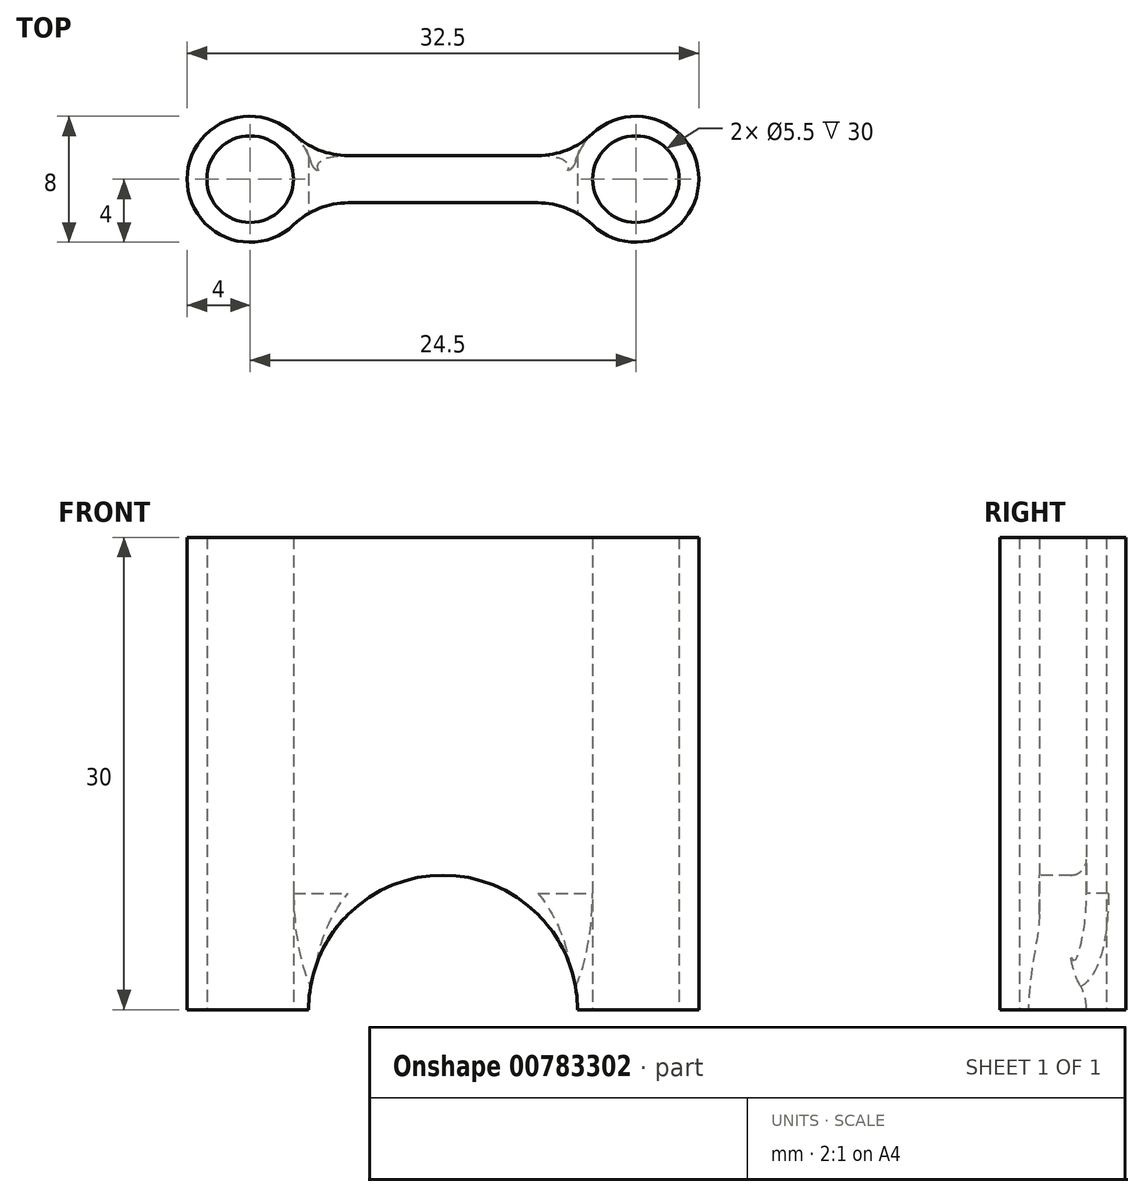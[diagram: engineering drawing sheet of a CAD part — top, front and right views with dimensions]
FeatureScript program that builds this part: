
annotation { "Feature Type Name" : "Feature", "Feature Type Description" : "" }
export const myFeature = defineFeature(function(context is Context, id is Id, definition is map)
    precondition{}
    {
        {
            var Q0;
            Q0=qCreatedBy(makeId("Top.planeOp"),FACE);
            var sketch = newSketch(context, id + "F0", { "sketchPlane" : qUnion([Q0])});
            skPoint(sketch, "E0", {"position": v(-12.25, 0) * mm});
            skPoint(sketch, "E1", {"position": v(12.25, 0) * mm});
            skCircle(sketch, "E2", {"center": v(-12.25, 0) * mm, "radius": 2.75 * mm});
            skCircle(sketch, "E3", {"center": v(12.25, 0) * mm, "radius": 2.75 * mm});
            skCircle(sketch, "E4", {"center": v(-12.25, 0) * mm, "radius": 4 * mm});
            skCircle(sketch, "E5", {"center": v(12.25, 0) * mm, "radius": 4 * mm});
            skLineSegment(sketch, "E6", {"start": v(-8.54, 1.5) * mm, "end": v(8.54, 1.5) * mm});
            skLineSegment(sketch, "E7", {"start": v(8.54, -1.5) * mm, "end": v(-8.54, -1.5) * mm});
            skPoint(sketch, "E8", {"position": v(-12.25, -4) * mm});
            skPoint(sketch, "E9", {"position": v(12.25, -4) * mm});
            skPoint(sketch, "E10", {"position": v(12.25, -8.25) * mm});
            skSolve(sketch);
        }
        {
            var Q0;
            Q0=makeQuery(id+"F0.imprint","IMPRINT",FACE,{"disambiguationData":[TD([[makeQuery(id+"F0.imprint","IMPRINT",EDGE,{"derivedFrom":sQuery(id+"F0.wireOp",EDGE,"E2")}),-1.0]])]});
            var Q1;
            Q1=makeQuery(id+"F0.imprint","IMPRINT",FACE,{"disambiguationData":[TD([[makeQuery(id+"F0.imprint","IMPRINT",EDGE,{"derivedFrom":sQuery(id+"F0.wireOp",EDGE,"E3")}),-1.0]])]});
            var Q2;
            {var subQ0=sQuery(id+"F0.wireOp",EDGE,"E6");Q2=makeQuery(id+"F0.imprint","IMPRINT",FACE,{"disambiguationData":[TD([[makeQuery(id+"F0.imprint","IMPRINT",EDGE,{"derivedFrom":subQ0}),-1.0]])]});}
            extrude(context, id + "F1", {"entities" : qUnion([Q0, Q1, Q2]), "depth" : 30 * mm, "offsetDistance" : 25 * mm});
        }
        {
            var Q0;
            Q0=makeQuery(id+"F1.opExtrude","SWEPT_FACE",FACE,{"disambiguationData":[OSD([sQuery(id+"F0.wireOp",EDGE,"E7")])]});
            var sketch = newSketch(context, id + "F2", { "sketchPlane" : qUnion([Q0])});
            skArc(sketch, "E11", {"start": v(8.54, 0) * mm, "mid": v(0, 8.54) * mm, "end": v(-8.54, 0) * mm});
            skArc(sketch, "E12", {"start": v(-9.91, 30) * mm, "mid": v(-0.01, 19.11) * mm, "end": v(9.9, 30) * mm});
            skSolve(sketch);
        }
        {
            var Q0;
            Q0=makeQuery(id+"F2.imprint","IMPRINT",FACE,{"disambiguationData":[TD([[makeQuery(id+"F2.imprint","IMPRINT",EDGE,{"derivedFrom":sQuery(id+"F2.wireOp",EDGE,"35eb756d-b366-46d8-bd96-28ccdfe76fae")}),1.0]])]});
            var Q1;
            Q1=makeQuery(id+"F2.imprint","IMPRINT",FACE,{"disambiguationData":[TD([[makeQuery(id+"F2.imprint","IMPRINT",EDGE,{"derivedFrom":sQuery(id+"F2.wireOp",EDGE,"E11")}),1.0]])]});
            extrude(context, id + "F3", {"entities" : qUnion([Q0, Q1]), "operationType" : NewBodyOperationType.REMOVE, "endBound" : BoundingType.THROUGH_ALL, "oppositeDirection" : true, "depth" : 25 * mm, "offsetDistance" : 25 * mm});
        }
        {
            var Q0;
            Q0=makeQuery(id+"F3.boolean.opBoolean","INTERSECT",EDGE,{"derivedFrom":[makeQuery(id+"F1.opExtrude","SWEPT_FACE",FACE,{"disambiguationData":[OSD([sQuery(id+"F0.wireOp",EDGE,"E6")])]}),makeQuery(id+"F3.opExtrude","SWEPT_FACE",FACE,{"disambiguationData":[OSD([sQuery(id+"F2.wireOp",EDGE,"35eb756d-b366-46d8-bd96-28ccdfe76fae")])]})]});
            var Q1;
            Q1=makeQuery(id+"F3.boolean.opBoolean","COPY",EDGE,{"derivedFrom":makeQuery(id+"F3.opExtrude","CAP_EDGE",EDGE,{"disambiguationData":[OSD([sQuery(id+"F2.wireOp",EDGE,"35eb756d-b366-46d8-bd96-28ccdfe76fae")])],"isStart":true})});
            var Q2;
            Q2=makeQuery(id+"F3.boolean.opBoolean","COPY",EDGE,{"derivedFrom":makeQuery(id+"F3.opExtrude","CAP_EDGE",EDGE,{"disambiguationData":[OSD([sQuery(id+"F2.wireOp",EDGE,"E11")])],"isStart":true})});
            var Q3;
            Q3=makeQuery(id+"F3.boolean.opBoolean","INTERSECT",EDGE,{"derivedFrom":[makeQuery(id+"F1.opExtrude","SWEPT_FACE",FACE,{"disambiguationData":[OSD([sQuery(id+"F0.wireOp",EDGE,"E6")])]}),makeQuery(id+"F3.opExtrude","SWEPT_FACE",FACE,{"disambiguationData":[OSD([sQuery(id+"F2.wireOp",EDGE,"E11")])]})]});
            fillet(context, id + "F4", {"entities" : qUnion([Q0, Q1, Q2, Q3]), "radius" : 1 * mm, "tangentPropagation" : true, "allowEdgeOverflow" : false});
        }
        {
            var Q0;
            Q0=makeQuery(id+"F1.opExtrude","SWEPT_EDGE",EDGE,{"disambiguationData":[OSD([sQuery(id+"F0.wireOp",EDGE,"E5"),sQuery(id+"F0.wireOp",EDGE,"E7")])]});
            var Q1;
            Q1=makeQuery(id+"F1.opExtrude","SWEPT_EDGE",EDGE,{"disambiguationData":[OSD([sQuery(id+"F0.wireOp",EDGE,"E4"),sQuery(id+"F0.wireOp",EDGE,"E7")])]});
            var Q2;
            Q2=makeQuery(id+"F1.opExtrude","SWEPT_EDGE",EDGE,{"disambiguationData":[OSD([sQuery(id+"F0.wireOp",EDGE,"E5"),sQuery(id+"F0.wireOp",EDGE,"E6")])]});
            var Q3;
            Q3=makeQuery(id+"F1.opExtrude","SWEPT_EDGE",EDGE,{"disambiguationData":[OSD([sQuery(id+"F0.wireOp",EDGE,"E4"),sQuery(id+"F0.wireOp",EDGE,"E6")])]});
            fillet(context, id + "F5", {"entities" : qUnion([Q0, Q1, Q2, Q3]), "radius" : 5 * mm, "tangentPropagation" : true, "allowEdgeOverflow" : false});
        }
    });
